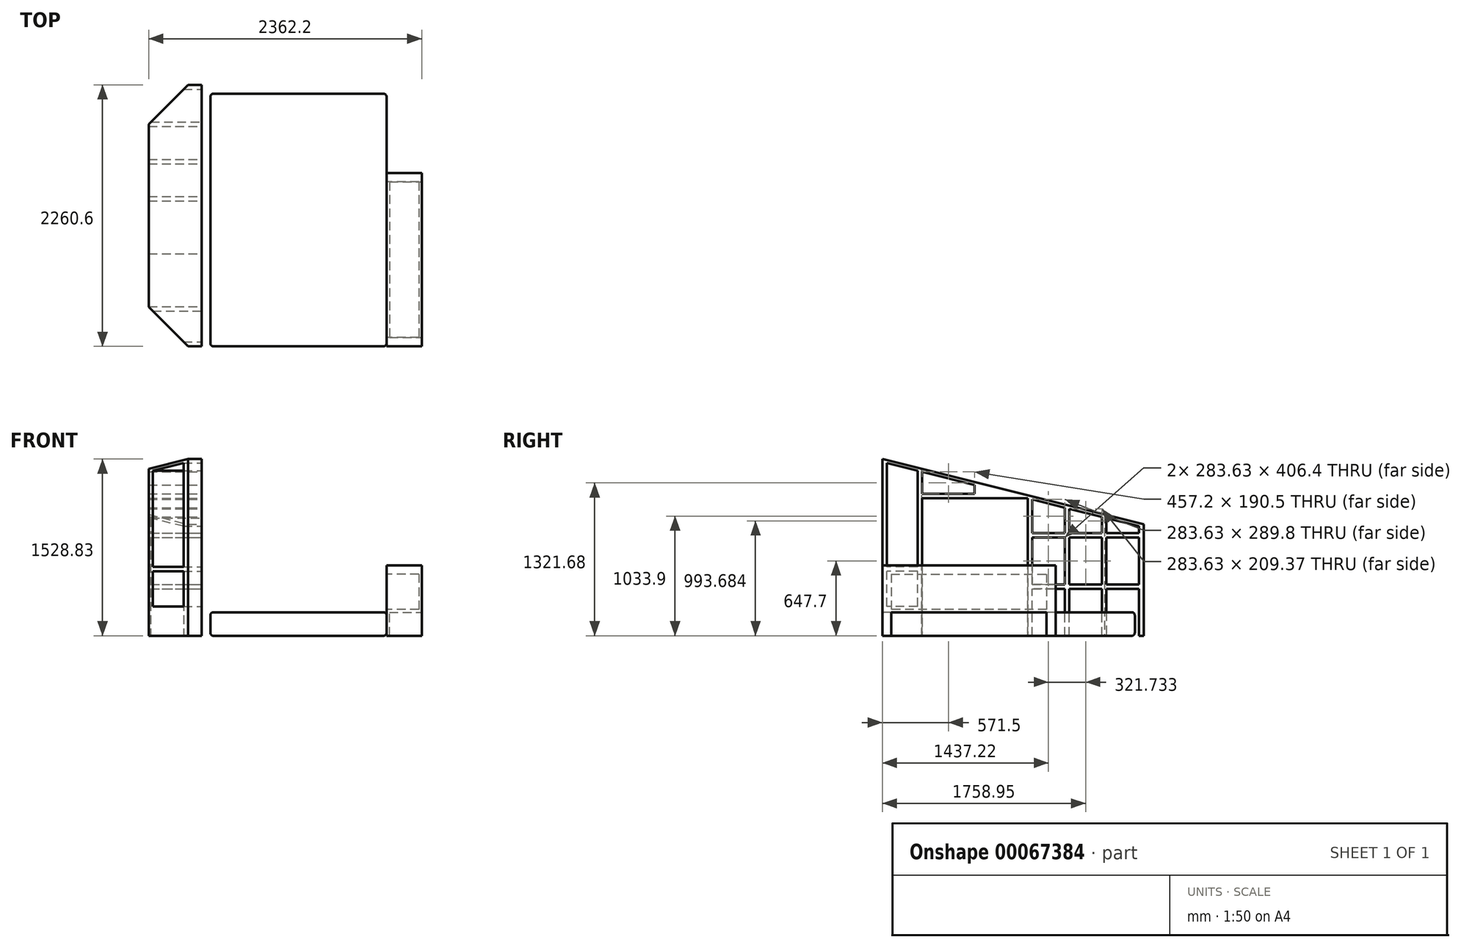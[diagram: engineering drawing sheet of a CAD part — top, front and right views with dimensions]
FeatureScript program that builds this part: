
annotation { "Feature Type Name" : "Feature", "Feature Type Description" : "" }
export const myFeature = defineFeature(function(context is Context, id is Id, definition is map)
    precondition{}
    {
        {
            var Q0;
            Q0=qCreatedBy(makeId("Right.planeOp"),FACE);
            var sketch = newSketch(context, id + "F0", { "sketchPlane" : qUnion([Q0])});
            skLineSegment(sketch, "E0", {"start": v(0, 0) * mm, "end": v(0, 609.6) * mm, "construction": true});
            skLineSegment(sketch, "E1", {"start": v(0, 609.6) * mm, "end": v(-762, 609.6) * mm, "construction": true});
            skLineSegment(sketch, "E2", {"start": v(-762, 609.6) * mm, "end": v(-762, 0) * mm});
            skLineSegment(sketch, "E3", {"start": v(-762, 0) * mm, "end": v(0, 0) * mm, "construction": true});
            skLineSegment(sketch, "E4", {"start": v(-762, 0) * mm, "end": v(-2260.6, 0) * mm});
            skLineSegment(sketch, "E5", {"start": v(-2260.6, 0) * mm, "end": v(-2260.6, 609.6) * mm});
            skLineSegment(sketch, "E6", {"start": v(-2260.6, 609.6) * mm, "end": v(-762, 609.6) * mm});
            skSolve(sketch);
        }
        {
            var Q0;
            Q0 = qSketchRegion(id + "F0", true);
            extrude(context, id + "F1", {"entities" : qUnion([Q0]), "oppositeDirection" : true, "depth" : 304.8 * mm});
        }
        {
            var Q0;
            Q0=makeQuery(id+"F1.opExtrude","CAP_FACE",FACE,{"disambiguationData":[OSD([sQuery(id+"F0.wireOp",EDGE,"E0"),sQuery(id+"F0.wireOp",EDGE,"E1"),sQuery(id+"F0.wireOp",EDGE,"E2"),sQuery(id+"F0.wireOp",EDGE,"E3")])],"isStart":false});
            var sketch = newSketch(context, id + "F2", { "sketchPlane" : qUnion([Q0])});
            skLineSegment(sketch, "E7", {"start": v(838.2, 228.6) * mm, "end": v(2184.4, 228.6) * mm});
            skLineSegment(sketch, "E8", {"start": v(2184.4, 533.4) * mm, "end": v(2184.4, 228.6) * mm});
            skLineSegment(sketch, "E9", {"start": v(2184.4, 533.4) * mm, "end": v(838.2, 533.4) * mm});
            skLineSegment(sketch, "E10", {"start": v(838.2, 533.4) * mm, "end": v(838.2, 228.6) * mm});
            skSolve(sketch);
        }
        {
            var Q0;
            Q0 = qSketchRegion(id + "F2", true);
            extrude(context, id + "F3", {"entities" : qUnion([Q0]), "operationType" : NewBodyOperationType.REMOVE, "oppositeDirection" : true, "depth" : 279.4 * mm});
        }
        {
            var Q0;
            Q0=makeQuery(id+"F1.opExtrude","CAP_FACE",FACE,{"disambiguationData":[OSD([sQuery(id+"F0.wireOp",EDGE,"E0"),sQuery(id+"F0.wireOp",EDGE,"E1"),sQuery(id+"F0.wireOp",EDGE,"E2"),sQuery(id+"F0.wireOp",EDGE,"E3")])],"isStart":true});
            var sketch = newSketch(context, id + "F4", { "sketchPlane" : qUnion([Q0])});
            skLineSegment(sketch, "E11.bottom", {"start": v(-2184.4, 0) * mm, "end": v(-838.2, 0) * mm});
            skLineSegment(sketch, "E11.top", {"start": v(-2184.4, 203.2) * mm, "end": v(-838.2, 203.2) * mm});
            skLineSegment(sketch, "E11.left", {"start": v(-2184.4, 0) * mm, "end": v(-2184.4, 203.2) * mm});
            skLineSegment(sketch, "E11.right", {"start": v(-838.2, 0) * mm, "end": v(-838.2, 203.2) * mm});
            skSolve(sketch);
        }
        {
            var Q0;
            Q0 = qSketchRegion(id + "F4", true);
            extrude(context, id + "F5", {"entities" : qUnion([Q0]), "operationType" : NewBodyOperationType.REMOVE, "oppositeDirection" : true, "depth" : 279.4 * mm});
        }
        {
            var Q0;
            Q0=qCreatedBy(makeId("Top.planeOp"),FACE);
            var sketch = newSketch(context, id + "F6", { "sketchPlane" : qUnion([Q0])});
            skLineSegment(sketch, "E12.bottom", {"start": v(-304.8, -76.2) * mm, "end": v(-1828.8, -76.2) * mm});
            skLineSegment(sketch, "E12.top", {"start": v(-304.8, -2260.6) * mm, "end": v(-1828.8, -2260.6) * mm});
            skLineSegment(sketch, "E12.left", {"start": v(-304.8, -76.2) * mm, "end": v(-304.8, -2260.6) * mm});
            skLineSegment(sketch, "E12.right", {"start": v(-1828.8, -76.2) * mm, "end": v(-1828.8, -2260.6) * mm});
            skSolve(sketch);
        }
        {
            var Q0;
            Q0 = qSketchRegion(id + "F6", true);
            extrude(context, id + "F7", {"entities" : qUnion([Q0]), "depth" : 203.2 * mm});
        }
        {
            var Q0;
            Q0=qCreatedBy(makeId("Top.planeOp"),FACE);
            var sketch = newSketch(context, id + "F8", { "sketchPlane" : qUnion([Q0])});
            skLineSegment(sketch, "E13", {"start": v(-1905, 0) * mm, "end": v(-1905, -2260.6) * mm});
            skLineSegment(sketch, "E14", {"start": v(-2362.2, -1921.15) * mm, "end": v(-2362.2, -339.45) * mm});
            skLineSegment(sketch, "E15", {"start": v(-2022.75, -2260.6) * mm, "end": v(-2362.2, -1921.15) * mm});
            skLineSegment(sketch, "E16", {"start": v(-2022.75, -2260.6) * mm, "end": v(-1905, -2260.6) * mm});
            skLineSegment(sketch, "E17", {"start": v(-1905, 0) * mm, "end": v(-2022.75, 0) * mm});
            skLineSegment(sketch, "E18", {"start": v(-2022.75, 0) * mm, "end": v(-2362.2, -339.45) * mm});
            skLineSegment(sketch, "E19", {"start": v(-2022.75, -2260.6) * mm, "end": v(-2022.75, -1921.15) * mm, "construction": true});
            skLineSegment(sketch, "E20", {"start": v(-2022.75, -1921.15) * mm, "end": v(-2362.2, -1921.15) * mm, "construction": true});
            skSolve(sketch);
        }
        {
            var Q0;
            Q0 = qSketchRegion(id + "F8", true);
            extrude(context, id + "F9", {"entities" : qUnion([Q0]), "depth" : 1574.8 * mm});
        }
        {
            var Q0;
            Q0=makeQuery(id+"F7.opExtrude","CAP_FACE",FACE,{"disambiguationData":[OSD([sQuery(id+"F6.wireOp",EDGE,"E12.bottom"),sQuery(id+"F6.wireOp",EDGE,"E12.top"),sQuery(id+"F6.wireOp",EDGE,"E12.left"),sQuery(id+"F6.wireOp",EDGE,"E12.right")])],"isStart":false});
            var Q1;
            Q1=makeQuery(id+"F7.opExtrude","SWEPT_EDGE",EDGE,{"disambiguationData":[OSD([sQuery(id+"F6.wireOp",EDGE,"E12.top"),sQuery(id+"F6.wireOp",EDGE,"E12.right")])]});
            var Q2;
            Q2=makeQuery(id+"F7.opExtrude","SWEPT_EDGE",EDGE,{"disambiguationData":[OSD([sQuery(id+"F6.wireOp",EDGE,"E12.top"),sQuery(id+"F6.wireOp",EDGE,"E12.left")])]});
            var Q3;
            Q3=makeQuery(id+"F7.opExtrude","SWEPT_EDGE",EDGE,{"disambiguationData":[OSD([sQuery(id+"F6.wireOp",EDGE,"E12.bottom"),sQuery(id+"F6.wireOp",EDGE,"E12.left")])]});
            var Q4;
            Q4=makeQuery(id+"F7.opExtrude","SWEPT_EDGE",EDGE,{"disambiguationData":[OSD([sQuery(id+"F6.wireOp",EDGE,"E12.bottom"),sQuery(id+"F6.wireOp",EDGE,"E12.right")])]});
            var Q5;
            Q5=makeQuery(id+"F7.opExtrude","CAP_FACE",FACE,{"disambiguationData":[OSD([sQuery(id+"F6.wireOp",EDGE,"E12.bottom"),sQuery(id+"F6.wireOp",EDGE,"E12.top"),sQuery(id+"F6.wireOp",EDGE,"E12.left"),sQuery(id+"F6.wireOp",EDGE,"E12.right")])],"isStart":true});
            fillet(context, id + "F10", {"entities" : qUnion([Q0, Q1, Q2, Q3, Q4, Q5]), "radius" : 25.4 * mm, "tangentPropagation" : true, "allowEdgeOverflow" : false});
        }
        {
            var Q0;
            Q0=makeQuery(id+"F9.opExtrude","SWEPT_FACE",FACE,{"disambiguationData":[OSD([sQuery(id+"F8.wireOp",EDGE,"E13")])]});
            var sketch = newSketch(context, id + "F11", { "sketchPlane" : qUnion([Q0])});
            skLineSegment(sketch, "E21", {"start": v(-2260.6, 1528.83) * mm, "end": v(0, 963.68) * mm});
            skLineSegment(sketch, "E22", {"start": v(0, 963.68) * mm, "end": v(0, 1574.8) * mm});
            skLineSegment(sketch, "E23", {"start": v(0, 1574.8) * mm, "end": v(-2260.6, 1574.8) * mm});
            skLineSegment(sketch, "E24", {"start": v(-2260.6, 1574.8) * mm, "end": v(-2260.6, 1528.83) * mm});
            skLineSegment(sketch, "E25", {"start": v(0, 963.68) * mm, "end": v(-304.8, 963.68) * mm, "construction": true});
            skLineSegment(sketch, "E26", {"start": v(-304.8, 1039.88) * mm, "end": v(-304.8, 963.68) * mm, "construction": true});
            skSolve(sketch);
        }
        {
            var Q0;
            Q0 = qSketchRegion(id + "F11", true);
            extrude(context, id + "F12", {"entities" : qUnion([Q0]), "operationType" : NewBodyOperationType.REMOVE, "endBound" : BoundingType.THROUGH_ALL, "oppositeDirection" : true, "depth" : 25.4 * mm});
        }
        {
            var Q0;
            Q0=makeQuery(id+"F9.opExtrude","SWEPT_FACE",FACE,{"disambiguationData":[OSD([sQuery(id+"F8.wireOp",EDGE,"E13")])]});
            var sketch = newSketch(context, id + "F13", { "sketchPlane" : qUnion([Q0])});
            skLineSegment(sketch, "E27.bottom", {"start": v(-2222.5, 558.8) * mm, "end": v(-1955.8, 558.8) * mm});
            skLineSegment(sketch, "E27.top", {"start": v(-2222.5, 254) * mm, "end": v(-1955.8, 254) * mm});
            skLineSegment(sketch, "E27.left", {"start": v(-2222.5, 558.8) * mm, "end": v(-2222.5, 254) * mm});
            skLineSegment(sketch, "E27.right", {"start": v(-1955.8, 558.8) * mm, "end": v(-1955.8, 254) * mm});
            skLineSegment(sketch, "E28", {"start": v(-2222.5, 596.9) * mm, "end": v(-1955.8, 596.9) * mm});
            skLineSegment(sketch, "E29", {"start": v(-1955.8, 596.9) * mm, "end": v(-1955.8, 1426.45) * mm});
            skLineSegment(sketch, "E30", {"start": v(-1955.8, 1426.45) * mm, "end": v(-2222.5, 1493.13) * mm});
            skLineSegment(sketch, "E31", {"start": v(-2222.5, 1493.13) * mm, "end": v(-2222.5, 596.9) * mm});
            skLineSegment(sketch, "E32", {"start": v(-321.73, 1017.94) * mm, "end": v(-321.73, 889) * mm});
            skLineSegment(sketch, "E33", {"start": v(-321.73, 889) * mm, "end": v(-38.1, 889) * mm});
            skLineSegment(sketch, "E34", {"start": v(-38.1, 889) * mm, "end": v(-38.1, 947.03) * mm});
            skLineSegment(sketch, "E35", {"start": v(-38.1, 947.03) * mm, "end": v(-321.73, 1017.94) * mm});
            skLineSegment(sketch, "E36.bottom", {"start": v(-321.73, 850.9) * mm, "end": v(-38.1, 850.9) * mm});
            skLineSegment(sketch, "E36.top", {"start": v(-321.73, 444.5) * mm, "end": v(-38.1, 444.5) * mm});
            skLineSegment(sketch, "E36.left", {"start": v(-321.73, 850.9) * mm, "end": v(-321.73, 444.5) * mm});
            skLineSegment(sketch, "E36.right", {"start": v(-38.1, 850.9) * mm, "end": v(-38.1, 444.5) * mm});
            skLineSegment(sketch, "E37.bottom", {"start": v(-321.73, 406.4) * mm, "end": v(-38.1, 406.4) * mm});
            skLineSegment(sketch, "E37.top", {"start": v(-321.73, 0) * mm, "end": v(-38.1, 0) * mm});
            skLineSegment(sketch, "E37.left", {"start": v(-321.73, 406.4) * mm, "end": v(-321.73, 0) * mm});
            skLineSegment(sketch, "E37.right", {"start": v(-38.1, 406.4) * mm, "end": v(-38.1, 0) * mm});
            skLineSegment(sketch, "E38.bottom", {"start": v(-1003.3, 0) * mm, "end": v(-1917.7, 0) * mm});
            skLineSegment(sketch, "E38.top", {"start": v(-1003.3, 1188.33) * mm, "end": v(-1917.7, 1188.33) * mm});
            skLineSegment(sketch, "E38.left", {"start": v(-1003.3, 0) * mm, "end": v(-1003.3, 1188.33) * mm});
            skLineSegment(sketch, "E38.right", {"start": v(-1917.7, 0) * mm, "end": v(-1917.7, 1188.33) * mm});
            skLineSegment(sketch, "E39.bottom", {"start": v(-359.83, 0) * mm, "end": v(-643.47, 0) * mm});
            skLineSegment(sketch, "E39.top", {"start": v(-359.83, 406.4) * mm, "end": v(-643.47, 406.4) * mm});
            skLineSegment(sketch, "E39.left", {"start": v(-359.83, 0) * mm, "end": v(-359.83, 406.4) * mm});
            skLineSegment(sketch, "E39.right", {"start": v(-643.47, 0) * mm, "end": v(-643.47, 406.4) * mm});
            skLineSegment(sketch, "E40.bottom", {"start": v(-681.57, 0) * mm, "end": v(-965.2, 0) * mm});
            skLineSegment(sketch, "E40.top", {"start": v(-681.57, 406.4) * mm, "end": v(-965.2, 406.4) * mm});
            skLineSegment(sketch, "E40.left", {"start": v(-681.57, 0) * mm, "end": v(-681.57, 406.4) * mm});
            skLineSegment(sketch, "E40.right", {"start": v(-965.2, 0) * mm, "end": v(-965.2, 406.4) * mm});
            skLineSegment(sketch, "E41.bottom", {"start": v(-359.83, 444.5) * mm, "end": v(-643.47, 444.5) * mm});
            skLineSegment(sketch, "E41.top", {"start": v(-359.83, 850.9) * mm, "end": v(-643.47, 850.9) * mm});
            skLineSegment(sketch, "E41.left", {"start": v(-359.83, 444.5) * mm, "end": v(-359.83, 850.9) * mm});
            skLineSegment(sketch, "E41.right", {"start": v(-643.47, 444.5) * mm, "end": v(-643.47, 850.9) * mm});
            skLineSegment(sketch, "E42.bottom", {"start": v(-681.57, 444.5) * mm, "end": v(-965.2, 444.5) * mm});
            skLineSegment(sketch, "E42.top", {"start": v(-681.57, 850.9) * mm, "end": v(-965.2, 850.9) * mm});
            skLineSegment(sketch, "E42.left", {"start": v(-681.57, 444.5) * mm, "end": v(-681.57, 850.9) * mm});
            skLineSegment(sketch, "E42.right", {"start": v(-965.2, 444.5) * mm, "end": v(-965.2, 850.9) * mm});
            skLineSegment(sketch, "E43.bottom", {"start": v(-359.83, 889) * mm, "end": v(-643.47, 889) * mm});
            skLineSegment(sketch, "E43.left", {"start": v(-359.83, 889) * mm, "end": v(-359.83, 1027.46) * mm});
            skLineSegment(sketch, "E43.right", {"start": v(-643.47, 889) * mm, "end": v(-643.47, 1098.37) * mm});
            skLineSegment(sketch, "E44", {"start": v(-681.57, 889) * mm, "end": v(-681.57, 1107.9) * mm});
            skLineSegment(sketch, "E45", {"start": v(-681.57, 1107.9) * mm, "end": v(-965.2, 1178.8) * mm});
            skLineSegment(sketch, "E46", {"start": v(-965.2, 1178.8) * mm, "end": v(-965.2, 889) * mm});
            skLineSegment(sketch, "E47", {"start": v(-965.2, 889) * mm, "end": v(-681.57, 889) * mm});
            skLineSegment(sketch, "E48", {"start": v(-643.47, 1098.37) * mm, "end": v(-359.83, 1027.46) * mm});
            skLineSegment(sketch, "E49", {"start": v(-1917.7, 1226.43) * mm, "end": v(-1460.5, 1226.43) * mm});
            skLineSegment(sketch, "E50", {"start": v(-1460.5, 1226.43) * mm, "end": v(-1460.5, 1302.63) * mm});
            skLineSegment(sketch, "E51", {"start": v(-1460.5, 1302.63) * mm, "end": v(-1917.7, 1416.93) * mm});
            skLineSegment(sketch, "E52", {"start": v(-1917.7, 1416.93) * mm, "end": v(-1917.7, 1226.43) * mm});
            skSolve(sketch);
        }
        {
            var Q0;
            Q0 = qSketchRegion(id + "F13", true);
            extrude(context, id + "F14", {"entities" : qUnion([Q0]), "operationType" : NewBodyOperationType.REMOVE, "endBound" : BoundingType.THROUGH_ALL, "oppositeDirection" : true, "depth" : 25.4 * mm});
        }
    });
